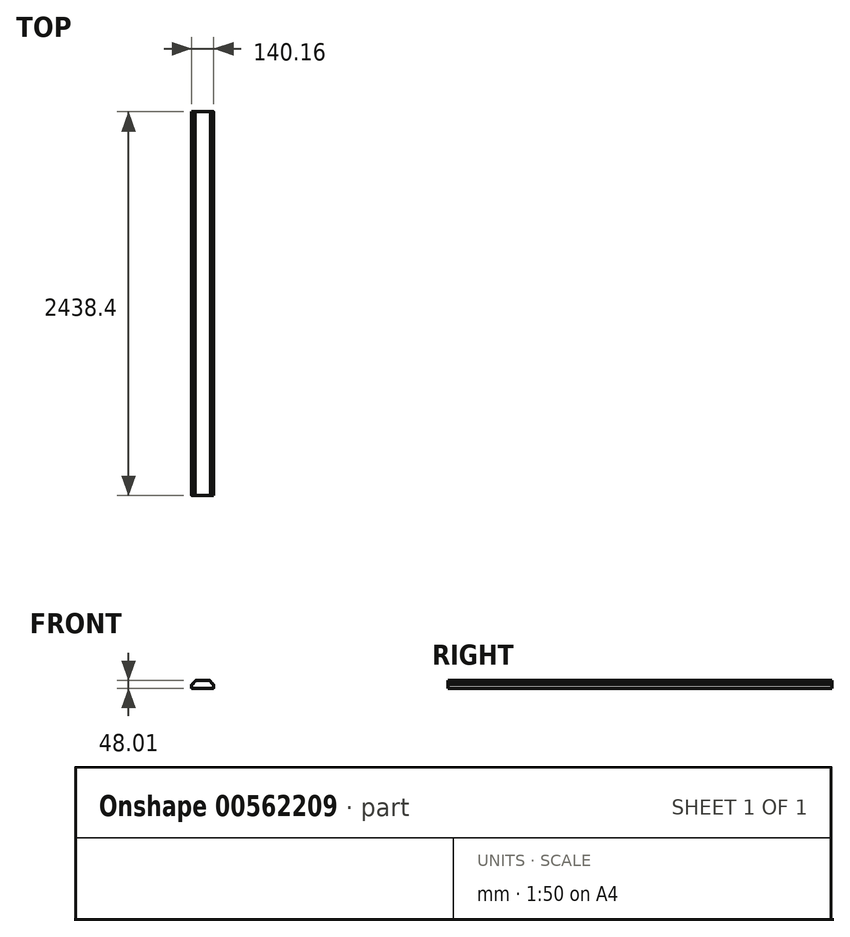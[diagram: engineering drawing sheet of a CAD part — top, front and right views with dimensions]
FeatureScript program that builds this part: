
annotation { "Feature Type Name" : "Feature", "Feature Type Description" : "" }
export const myFeature = defineFeature(function(context is Context, id is Id, definition is map)
    precondition{}
    {
        {
            var Q0;
            Q0=qCreatedBy(makeId("Front.planeOp"),FACE);
            var sketch = newSketch(context, id + "F0", { "sketchPlane" : qUnion([Q0])});
            skLineSegment(sketch, "E0.bottom", {"start": v(-3.17, 0) * mm, "end": v(-136.53, 0) * mm});
            skLineSegment(sketch, "E0.top", {"start": v(-24.6, 48) * mm, "end": v(-115.1, 48) * mm});
            skLineSegment(sketch, "E0.left", {"start": v(0, 3.18) * mm, "end": v(0, 20.96) * mm});
            skLineSegment(sketch, "E0.right", {"start": v(-139.7, 3.18) * mm, "end": v(-139.7, 20.96) * mm});
            skLineSegment(sketch, "E1.0", {"start": v(-4.32, 24.13) * mm, "end": v(-4.32, 26.67) * mm});
            skLineSegment(sketch, "E2.0", {"start": v(-12.7, 34.6) * mm, "end": v(-12.7, 35.81) * mm});
            skLineSegment(sketch, "E3.0", {"start": v(-3.17, 24.13) * mm, "end": v(-4.32, 24.13) * mm});
            skLineSegment(sketch, "E4.0", {"start": v(-4.32, 26.67) * mm, "end": v(-4.76, 26.67) * mm});
            skLineSegment(sketch, "E5.0", {"start": v(-19.05, 43.94) * mm, "end": v(-21.43, 43.94) * mm});
            skLineSegment(sketch, "E6.trimOffspring", {"start": v(-12.7, 35.81) * mm, "end": v(-12.7, 35.81) * mm});
            skLineSegment(sketch, "E7.trimOffspring", {"start": v(-21.43, 43.94) * mm, "end": v(-21.43, 44.83) * mm});
            skLineSegment(sketch, "E8.trimOffspring", {"start": v(-19.05, 42.16) * mm, "end": v(-19.05, 43.94) * mm});
            skPoint(sketch, "E9.visualSharp", {"position": v(-21.43, 48) * mm});
            skArc(sketch, "E9.filletArc", {"start": v(-21.43, 44.83) * mm, "mid": v(-22.36, 47.08) * mm, "end": v(-24.6, 48) * mm});
            skPoint(sketch, "E10.visualSharp", {"position": v(-19.05, 35.81) * mm});
            skArc(sketch, "E10.filletArc", {"start": v(-19.05, 42.16) * mm, "mid": v(-17.2, 37.67) * mm, "end": v(-12.7, 35.81) * mm});
            skPoint(sketch, "E11.visualSharp", {"position": v(-12.7, 26.67) * mm});
            skArc(sketch, "E11.filletArc", {"start": v(-12.7, 34.6) * mm, "mid": v(-10.38, 29) * mm, "end": v(-4.76, 26.67) * mm});
            skPoint(sketch, "E12.visualSharp", {"position": v(0, 24.13) * mm});
            skArc(sketch, "E12.filletArc", {"start": v(0, 20.96) * mm, "mid": v(-0.93, 23.2) * mm, "end": v(-3.17, 24.13) * mm});
            skLineSegment(sketch, "E13.MirrorCS", {"start": v(-127, 34.6) * mm, "end": v(-127, 35.81) * mm});
            skLineSegment(sketch, "E14.MirrorCS", {"start": v(-120.65, 42.16) * mm, "end": v(-120.65, 43.94) * mm});
            skLineSegment(sketch, "E15.MirrorCS", {"start": v(-118.27, 43.94) * mm, "end": v(-118.27, 44.83) * mm});
            skLineSegment(sketch, "E16.MirrorCS", {"start": v(-120.65, 43.94) * mm, "end": v(-118.27, 43.94) * mm});
            skLineSegment(sketch, "E17.MirrorCS", {"start": v(-135.38, 24.13) * mm, "end": v(-135.38, 26.67) * mm});
            skLineSegment(sketch, "E18.MirrorCS", {"start": v(-135.38, 26.67) * mm, "end": v(-134.94, 26.67) * mm});
            skLineSegment(sketch, "E19.MirrorCS", {"start": v(-136.53, 24.13) * mm, "end": v(-135.38, 24.13) * mm});
            skArc(sketch, "E20.MirrorCS", {"start": v(-118.27, 44.83) * mm, "mid": v(-117.34, 47.08) * mm, "end": v(-115.1, 48) * mm});
            skArc(sketch, "E21.MirrorCS", {"start": v(-139.7, 20.96) * mm, "mid": v(-138.77, 23.2) * mm, "end": v(-136.53, 24.13) * mm});
            skArc(sketch, "E22.MirrorCS", {"start": v(-127, 34.6) * mm, "mid": v(-129.32, 29) * mm, "end": v(-134.94, 26.67) * mm});
            skArc(sketch, "E23.MirrorCS", {"start": v(-120.65, 42.16) * mm, "mid": v(-122.5, 37.67) * mm, "end": v(-127, 35.81) * mm});
            skPoint(sketch, "E24.MirrorP", {"position": v(-139.7, 24.13) * mm});
            skLineSegment(sketch, "E25.MirrorCS", {"start": v(-127, 35.81) * mm, "end": v(-127, 35.81) * mm});
            skPoint(sketch, "E26.MirrorP", {"position": v(-127, 26.67) * mm});
            skPoint(sketch, "E27.MirrorP", {"position": v(-120.65, 35.81) * mm});
            skPoint(sketch, "E28.MirrorP", {"position": v(-118.27, 48) * mm});
            skPoint(sketch, "E29.start.orphan", {"position": v(-69.85, 0) * mm});
            skPoint(sketch, "E30.visualSharp", {"position": v(-139.7, 0) * mm});
            skArc(sketch, "E30.filletArc", {"start": v(-139.7, 3.18) * mm, "mid": v(-138.77, 0.93) * mm, "end": v(-136.53, 0) * mm});
            skPoint(sketch, "E31.visualSharp", {"position": v(0, 0) * mm});
            skArc(sketch, "E31.filletArc", {"start": v(-3.17, 0) * mm, "mid": v(-0.93, 0.93) * mm, "end": v(0, 3.18) * mm});
            skSolve(sketch);
        }
        {
            var Q0;
            Q0=makeQuery(id+"F0.imprint","IMPRINT",FACE,{"disambiguationData":[TD([[makeQuery(id+"F0.imprint","IMPRINT",EDGE,{"derivedFrom":sQuery(id+"F0.wireOp",EDGE,"E0.bottom")}),-1.0]])]});
            extrude(context, id + "F1", {"entities" : qUnion([Q0]), "oppositeDirection" : true, "depth" : 2438.4 * mm, "offsetDistance" : 25.4 * mm});
        }
        {
            var Q0;
            Q0=qCreatedBy(makeId("Front.planeOp"),FACE);
            var sketch = newSketch(context, id + "F2", { "sketchPlane" : qUnion([Q0])});
            skArc(sketch, "E32", {"start": v(-135.86, 24.43) * mm, "mid": v(-138.74, 23.24) * mm, "end": v(-139.93, 20.36) * mm});
            skArc(sketch, "E33", {"start": v(-135.86, 27.1) * mm, "mid": v(-130.44, 30.57) * mm, "end": v(-127.62, 36.34) * mm});
            skArc(sketch, "E34", {"start": v(-127.62, 36.34) * mm, "mid": v(-122.93, 39.32) * mm, "end": v(-120.2, 44.16) * mm});
            skArc(sketch, "E35", {"start": v(-113.87, 48) * mm, "mid": v(-116.67, 46.9) * mm, "end": v(-117.93, 44.16) * mm});
            skLineSegment(sketch, "E36", {"start": v(-120.2, 44.16) * mm, "end": v(-117.93, 44.16) * mm});
            skLineSegment(sketch, "E37", {"start": v(-135.86, 24.43) * mm, "end": v(-133.13, 24.43) * mm, "construction": true});
            skLineSegment(sketch, "E38", {"start": v(-135.86, 24.43) * mm, "end": v(-135.86, 27.1) * mm});
            skLineSegment(sketch, "E39", {"start": v(-139.93, 20.36) * mm, "end": v(-139.93, 0) * mm});
            skLineSegment(sketch, "E40", {"start": v(-69.85, 0) * mm, "end": v(-139.93, 0) * mm});
            skLineSegment(sketch, "E41", {"start": v(-69.85, 48) * mm, "end": v(-69.85, 0) * mm});
            skLineSegment(sketch, "E42", {"start": v(-113.87, 48) * mm, "end": v(-69.85, 48) * mm});
            skLineSegment(sketch, "E43.MirrorCS", {"start": v(-19.5, 44.16) * mm, "end": v(-21.77, 44.16) * mm});
            skLineSegment(sketch, "E44.MirrorCS", {"start": v(-3.84, 24.43) * mm, "end": v(-3.84, 27.1) * mm});
            skLineSegment(sketch, "E45.MirrorCS", {"start": v(-3.84, 24.43) * mm, "end": v(-6.57, 24.43) * mm, "construction": true});
            skArc(sketch, "E46.MirrorCS", {"start": v(-3.84, 24.43) * mm, "mid": v(-0.96, 23.24) * mm, "end": v(0.23, 20.36) * mm});
            skArc(sketch, "E47.MirrorCS", {"start": v(-3.84, 27.1) * mm, "mid": v(-9.26, 30.57) * mm, "end": v(-12.08, 36.34) * mm});
            skArc(sketch, "E48.MirrorCS", {"start": v(-12.08, 36.34) * mm, "mid": v(-16.77, 39.32) * mm, "end": v(-19.5, 44.16) * mm});
            skArc(sketch, "E49.MirrorCS", {"start": v(-25.83, 48) * mm, "mid": v(-23.03, 46.9) * mm, "end": v(-21.77, 44.16) * mm});
            skLineSegment(sketch, "E50.MirrorCS", {"start": v(0.23, 20.36) * mm, "end": v(0.23, 0) * mm});
            skLineSegment(sketch, "E51.MirrorCS", {"start": v(-69.85, 0) * mm, "end": v(0.23, 0) * mm});
            skLineSegment(sketch, "E52.MirrorCS", {"start": v(-25.83, 48) * mm, "end": v(-69.85, 48) * mm});
            skSolve(sketch);
        }
        {
            var Q0;
            Q0 = qSketchRegion(id + "F2", true);
            var Q1;
            Q1=makeQuery(id+"F1.opExtrude","CAP_FACE",FACE,{"disambiguationData":[OSD([sQuery(id+"F0.wireOp",EDGE,"E0.bottom"),sQuery(id+"F0.wireOp",EDGE,"E0.top"),sQuery(id+"F0.wireOp",EDGE,"E0.left"),sQuery(id+"F0.wireOp",EDGE,"E0.right"),sQuery(id+"F0.wireOp",EDGE,"E1.0"),sQuery(id+"F0.wireOp",EDGE,"E2.0"),sQuery(id+"F0.wireOp",EDGE,"E3.0"),sQuery(id+"F0.wireOp",EDGE,"E4.0"),sQuery(id+"F0.wireOp",EDGE,"E5.0"),sQuery(id+"F0.wireOp",EDGE,"E7.trimOffspring"),sQuery(id+"F0.wireOp",EDGE,"E8.trimOffspring"),sQuery(id+"F0.wireOp",EDGE,"E9.filletArc"),sQuery(id+"F0.wireOp",EDGE,"E10.filletArc"),sQuery(id+"F0.wireOp",EDGE,"E11.filletArc"),sQuery(id+"F0.wireOp",EDGE,"E12.filletArc"),sQuery(id+"F0.wireOp",EDGE,"E13.MirrorCS"),sQuery(id+"F0.wireOp",EDGE,"E14.MirrorCS"),sQuery(id+"F0.wireOp",EDGE,"E15.MirrorCS"),sQuery(id+"F0.wireOp",EDGE,"E16.MirrorCS"),sQuery(id+"F0.wireOp",EDGE,"E17.MirrorCS"),sQuery(id+"F0.wireOp",EDGE,"E18.MirrorCS"),sQuery(id+"F0.wireOp",EDGE,"E19.MirrorCS"),sQuery(id+"F0.wireOp",EDGE,"E20.MirrorCS"),sQuery(id+"F0.wireOp",EDGE,"E21.MirrorCS"),sQuery(id+"F0.wireOp",EDGE,"E22.MirrorCS"),sQuery(id+"F0.wireOp",EDGE,"E23.MirrorCS"),sQuery(id+"F0.wireOp",EDGE,"E30.filletArc"),sQuery(id+"F0.wireOp",EDGE,"E31.filletArc")])],"isStart":false});
            extrude(context, id + "F3", {"entities" : qUnion([Q0]), "endBound" : BoundingType.UP_TO_SURFACE, "oppositeDirection" : true, "depth" : 25.4 * mm, "endBoundEntityFace" : qUnion([Q1]), "offsetDistance" : 25.4 * mm});
        }
    });
